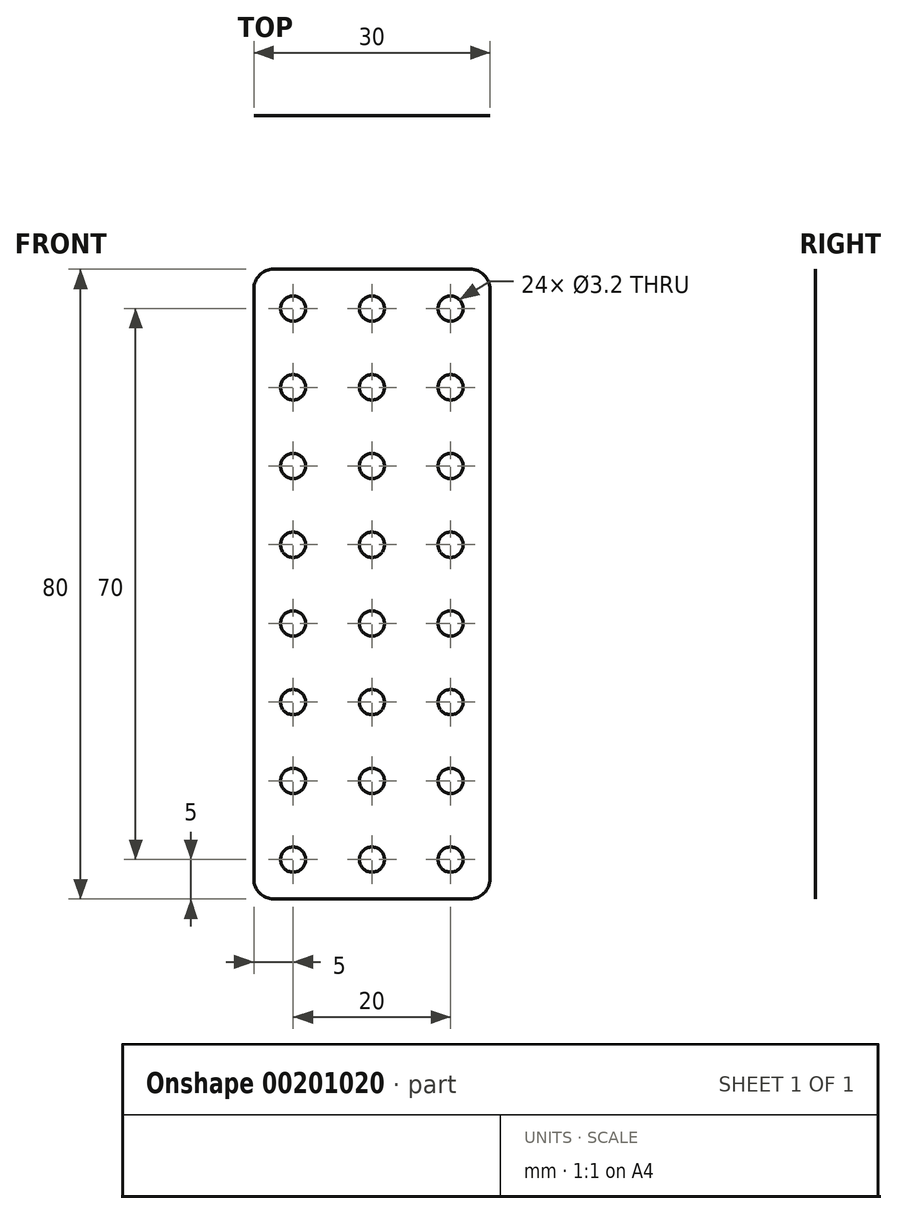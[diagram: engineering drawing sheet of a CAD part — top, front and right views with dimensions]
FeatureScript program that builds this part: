
annotation { "Feature Type Name" : "Feature", "Feature Type Description" : "" }
export const myFeature = defineFeature(function(context is Context, id is Id, definition is map)
    precondition{}
    {
        {
            var Q0;
            Q0=qCreatedBy(makeId("Front.planeOp"),FACE);
            var sketch = newSketch(context, id + "F0", { "sketchPlane" : qUnion([Q0])});
            skLineSegment(sketch, "E0.bottom", {"start": v(2.54, 0) * mm, "end": v(27.46, 0) * mm});
            skLineSegment(sketch, "E0.top", {"start": v(2.54, -80) * mm, "end": v(27.46, -80) * mm});
            skLineSegment(sketch, "E0.left", {"start": v(0, -2.54) * mm, "end": v(0, -77.46) * mm});
            skLineSegment(sketch, "E0.right", {"start": v(30, -2.54) * mm, "end": v(30, -77.46) * mm});
            skPoint(sketch, "E1.visualSharp", {"position": v(0, 0) * mm});
            skArc(sketch, "E1.filletArc", {"start": v(2.54, 0) * mm, "mid": v(0.74, -0.74) * mm, "end": v(0, -2.54) * mm});
            skPoint(sketch, "E2.visualSharp", {"position": v(30, 0) * mm});
            skArc(sketch, "E2.filletArc", {"start": v(30, -2.54) * mm, "mid": v(29.26, -0.74) * mm, "end": v(27.46, 0) * mm});
            skPoint(sketch, "E3.visualSharp", {"position": v(30, -80) * mm});
            skArc(sketch, "E3.filletArc", {"start": v(27.46, -80) * mm, "mid": v(29.26, -79.26) * mm, "end": v(30, -77.46) * mm});
            skPoint(sketch, "E4.visualSharp", {"position": v(0, -80) * mm});
            skArc(sketch, "E4.filletArc", {"start": v(0, -77.46) * mm, "mid": v(0.74, -79.26) * mm, "end": v(2.54, -80) * mm});
            skCircle(sketch, "E5", {"center": v(5, -5) * mm, "radius": 1.6 * mm});
            skCircle(sketch, "E6.0.1.0", {"center": v(5, -15) * mm, "radius": 1.6 * mm});
            skCircle(sketch, "E6.0.2.0", {"center": v(5, -25) * mm, "radius": 1.6 * mm});
            skCircle(sketch, "E6.0.3.0", {"center": v(5, -35) * mm, "radius": 1.6 * mm});
            skCircle(sketch, "E6.0.4.0", {"center": v(5, -45) * mm, "radius": 1.6 * mm});
            skCircle(sketch, "E6.0.5.0", {"center": v(5, -55) * mm, "radius": 1.6 * mm});
            skCircle(sketch, "E6.0.6.0", {"center": v(5, -65) * mm, "radius": 1.6 * mm});
            skCircle(sketch, "E6.0.7.0", {"center": v(5, -75) * mm, "radius": 1.6 * mm});
            skCircle(sketch, "E6.1.0.0", {"center": v(15, -5) * mm, "radius": 1.6 * mm});
            skCircle(sketch, "E6.1.1.0", {"center": v(15, -15) * mm, "radius": 1.6 * mm});
            skCircle(sketch, "E6.1.2.0", {"center": v(15, -25) * mm, "radius": 1.6 * mm});
            skCircle(sketch, "E6.1.3.0", {"center": v(15, -35) * mm, "radius": 1.6 * mm});
            skCircle(sketch, "E6.1.4.0", {"center": v(15, -45) * mm, "radius": 1.6 * mm});
            skCircle(sketch, "E6.1.5.0", {"center": v(15, -55) * mm, "radius": 1.6 * mm});
            skCircle(sketch, "E6.1.6.0", {"center": v(15, -65) * mm, "radius": 1.6 * mm});
            skCircle(sketch, "E6.1.7.0", {"center": v(15, -75) * mm, "radius": 1.6 * mm});
            skCircle(sketch, "E6.2.0.0", {"center": v(25, -5) * mm, "radius": 1.6 * mm});
            skCircle(sketch, "E6.2.1.0", {"center": v(25, -15) * mm, "radius": 1.6 * mm});
            skCircle(sketch, "E6.2.2.0", {"center": v(25, -25) * mm, "radius": 1.6 * mm});
            skCircle(sketch, "E6.2.3.0", {"center": v(25, -35) * mm, "radius": 1.6 * mm});
            skCircle(sketch, "E6.2.4.0", {"center": v(25, -45) * mm, "radius": 1.6 * mm});
            skCircle(sketch, "E6.2.5.0", {"center": v(25, -55) * mm, "radius": 1.6 * mm});
            skCircle(sketch, "E6.2.6.0", {"center": v(25, -65) * mm, "radius": 1.6 * mm});
            skCircle(sketch, "E6.2.7.0", {"center": v(25, -75) * mm, "radius": 1.6 * mm});
            skLineSegment(sketch, "E6.direction1", {"start": v(5, -5) * mm, "end": v(15, -5) * mm, "construction": true});
            skLineSegment(sketch, "E6.direction2", {"start": v(5, -5) * mm, "end": v(5, -15) * mm, "construction": true});
            skSolve(sketch);
        }
        {
            var Q0;
            Q0=makeQuery(id+"F0.imprint","IMPRINT",FACE,{"disambiguationData":[TD([[makeQuery(id+"F0.imprint","IMPRINT",EDGE,{"derivedFrom":sQuery(id+"F0.wireOp",EDGE,"E0.bottom")}),-1.0]])]});
            extrude(context, id + "F1", {"entities" : qUnion([Q0]), "depth" : 1 / 203.2 * mm});
        }
    });
